FCSTD DOCUMENT  (FreeCAD 1.1R38827 (Git))
Label: composit_stand3_bar_assembly
License: All rights reserved
LicenseURL: http://en.wikipedia.org/wiki/All_rights_reserved
objects: App::Link×4, App::DocumentObjectGroup×3, PartDesign::CoordinateSystem×2, App::FeaturePython×1, App::Part×1
note: 2 computed .brp shape members not serialized (recipe doc carries the construction recipe); baked Part::Feature solids carry a one-line shape summary decoded from their .brp
EXTERNAL_REF file=composit_stand3_bar_model.FCStd obj=Local_CS
EXTERNAL_REF file=composit_stand3_bar_model.FCStd obj=Body
EXTERNAL_REF file=composit_stand3_bar_bottom_model.FCStd obj=Local_CS
EXTERNAL_REF file=composit_stand3_bar_model.FCStd obj=Local_CS001
EXTERNAL_REF file=composit_stand3_bar_bottom_model.FCStd obj=Body
EXTERNAL_REF file=composit_stand3_bar_bottom_model.FCStd obj=Local_CS001
EXTERNAL_REF file=composit_stand3_bar_model.FCStd obj=Local_CS002
EXTERNAL_REF file=composit_stand3_bar_bottom_model.FCStd obj=Body002
EXTERNAL_REF file=composit_stand3_bar_model.FCStd obj=Local_CS004
EXTERNAL_REF file=composit_stand3_bar_top_model.FCStd obj=Local_CS001
EXTERNAL_REF file=composit_stand3_bar_top_model.FCStd obj=Body
EXTERNAL_REF file=composit_stand3_bar_main.FCStd obj=Spreadsheet

FEATURE [App::DocumentObjectGroup] Parts
FEATURE [PartDesign::CoordinateSystem] LCS_Origin
  AttacherType = Attacher::AttachEngine3D
  AttachmentSupport = -> [X_Axis]
  MapMode = 2
FEATURE [App::DocumentObjectGroup] Constraints
FEATURE [App::FeaturePython] Variables  # WARN: FeaturePython — macro-defined, semantics opaque (R4)
  Type = App::PropertyContainer
FEATURE [App::DocumentObjectGroup] Configurations
FEATURE [App::Link] bar001
  AttachedBy = #Local_CS
  AttachedTo = Parent Assembly#LCS_Origin
  LinkedObject = -> <external composit_stand3_bar_model.FCStd>#Body
  SolverId = Asm4EE
  expr: Placement = LCS_Origin.Placement * AttachmentOffset * composit_stand3_bar_model#Local_CS.Placement ^ -1
FEATURE [App::Link] bar_bottom
  AttachedBy = #Local_CS
  AttachedTo = bar001#Local_CS001
  LinkPlacement = pos=(54,18.3,0) rot=(0,0,1;1.5708rad)
  LinkedObject = -> <external composit_stand3_bar_bottom_model.FCStd>#Body
  Placement = pos=(54,18.3,0) rot=(0,0,1;1.5708rad)
  SolverId = Asm4EE
  expr: Placement = bar001.Placement * composit_stand3_bar_model#Local_CS001.Placement * AttachmentOffset * composit_stand3_bar_bottom_model#Local_CS.Placement ^ -1
FEATURE [App::Link] bar_bottom_mirror
  AttachedBy = #Local_CS001
  AttachedTo = bar001#Local_CS002
  LinkPlacement = pos=(54,-18.3,0) rot=(0,0,-1;1.5708rad)
  LinkedObject = -> <external composit_stand3_bar_bottom_model.FCStd>#Body002
  Placement = pos=(54,-18.3,0) rot=(0,0,-1;1.5708rad)
  SolverId = Asm4EE
  expr: Placement = bar001.Placement * composit_stand3_bar_model#Local_CS002.Placement * AttachmentOffset * composit_stand3_bar_bottom_model#Local_CS001.Placement ^ -1
FEATURE [App::Link] top
  AttachedBy = #Local_CS001
  AttachedTo = bar001#Local_CS004
  AttachmentOffset = pos=(0,0,-6) rot=(0,0,1;0rad)
  LinkPlacement = pos=(2,0,1594) rot=(0,0,1;0rad)
  LinkedObject = -> <external composit_stand3_bar_top_model.FCStd>#Body
  Placement = pos=(2,0,1594) rot=(0,0,1;0rad)
  SolverId = Asm4EE
  expr: Placement = bar001.Placement * composit_stand3_bar_model#Local_CS004.Placement * AttachmentOffset * composit_stand3_bar_top_model#Local_CS001.Placement ^ -1
FEATURE [PartDesign::CoordinateSystem] top_LCS
  AttacherType = Attacher::AttachEngine3D
  AttachmentOffset = pos=(0,0,1684) rot=(0,0,1;0rad)
  AttachmentSupport = -> [LCS_Origin]
  MapMode = 5
  Placement = pos=(0,0,1684) rot=(0,0,1;0rad)
  expr: .AttachmentOffset.Base.z = composit_stand3_bar_main#<<Properties>>.height
FEATURE [App::Part] Assembly
  AssemblyType = Part::Link
  Group = -> [LCS_Origin,Constraints,Variables,Configurations,bar001,bar_bottom,bar_bottom_mirror,top,top_LCS]
  Origin = -> Origin
  Type = Assembly

RESOLVED EXTERNAL PARTS (link-assembly join: the EXTERNAL_REF files above that resolve inside this repo's crawl, each included once):
---- part composit_stand3_bar_bottom_model.FCStd = doc fcstd_6c99a19c1178 ----
FCSTD DOCUMENT  (FreeCAD 1.1R38827 (Git))
Label: composit_stand3_bar_bottom_model
License: All rights reserved
LicenseURL: http://en.wikipedia.org/wiki/All_rights_reserved
objects: PartDesign::SubShapeBinder×3, PartDesign::Pad×3, Part::FeaturePython×3, PartDesign::Body×3, App::Link×2, Part::Cylinder×2, PartDesign::CoordinateSystem×2, Part::Mirroring×2, Part::MultiFuse×1, PartDesign::Boolean×1, PartDesign::FeatureBase×1, Part::Feature×1
note: 30 computed .brp shape members not serialized (recipe doc carries the construction recipe); baked Part::Feature solids carry a one-line shape summary decoded from their .brp
EXTERNAL_REF file=composit_stand3_bar_bottom_main.FCStd obj=Sketch
EXTERNAL_REF file=composit_stand3_bar_bottom_main.FCStd obj=Sketch001
EXTERNAL_REF file=composit_stand3_bar_bottom_main.FCStd obj=Sketch002
EXTERNAL_REF file=composit_stand3_bar_bottom_main.FCStd obj=Spreadsheet
EXTERNAL_REF file=composit_stand3_bar_bottom_main.FCStd obj=Join
EXTERNAL_REF file=composit_stand3_bar_bottom_main.FCStd obj=Join001

FEATURE [PartDesign::SubShapeBinder] Binder
  BindCopyOnChange = 0
  BindMode = 0
  ClaimChildren = true
  Context = -> Body [Binder.]
  Fuse = false
  MakeFace = true
  OffsetFill = false
  OffsetIntersection = false
  OffsetJoinType = 0
  OffsetOpenResult = false
  PartialLoad = false
  Relative = true
  Support = -> [<external composit_stand3_bar_bottom_main.FCStd>#Sketch]
  _Version = 2
FEATURE [PartDesign::SubShapeBinder] Binder001
  BindCopyOnChange = 0
  BindMode = 0
  ClaimChildren = true
  Context = -> Body [Binder001.]
  Fuse = false
  MakeFace = true
  OffsetFill = false
  OffsetIntersection = false
  OffsetJoinType = 0
  OffsetOpenResult = false
  PartialLoad = false
  Relative = true
  Support = -> [<external composit_stand3_bar_bottom_main.FCStd>#Sketch001]
  _Version = 2
FEATURE [PartDesign::SubShapeBinder] Binder002
  BindCopyOnChange = 0
  BindMode = 0
  ClaimChildren = true
  Context = -> Body [Binder002.]
  Fuse = false
  MakeFace = true
  OffsetFill = false
  OffsetIntersection = false
  OffsetJoinType = 0
  OffsetOpenResult = false
  PartialLoad = false
  Relative = true
  Support = -> [<external composit_stand3_bar_bottom_main.FCStd>#Sketch002]
  _Version = 2
FEATURE [PartDesign::Pad] Pad
  Direction = (0,1,0)
  Length = 100
  Length2 = 10
  Midplane = true
  Profile = -> Binder
  Suppressed = false
  Type = 0
  expr: Length = <<composit_stand3_bar_bottom_main>>#<<Properties>>.width
FEATURE [PartDesign::Pad] Pad001
  BaseFeature = -> Pad
  Direction = (0,0,1)
  Length = 2
  Length2 = 10
  Profile = -> Binder001
  Suppressed = false
  Type = 0
  expr: Length = <<composit_stand3_bar_bottom_main>>#<<Properties>>.thickness
FEATURE [PartDesign::Pad] Pad002
  BaseFeature = -> Pad001
  Direction = (1,4e-16,0)
  Length = 2
  Length2 = 10
  Profile = -> Binder002
  Refine = true
  Suppressed = false
  Type = 0
  expr: Length = <<composit_stand3_bar_bottom_main>>#<<Properties>>.thickness
FEATURE [App::Link] Link  label="Join"
  LinkedObject = -> <external composit_stand3_bar_bottom_main.FCStd>#Join
FEATURE [App::Link] Link001  label="Join001"
  LinkedObject = -> <external composit_stand3_bar_bottom_main.FCStd>#Join001
FEATURE [Part::Cylinder] Cylinder  label="hole_3.4mm"
  Angle = 360
  AttacherType = Attacher::AttachEngine3D
  FirstAngle = 0
  Height = 10
  Placement = pos=(0,0,0) rot=(1,0,0;3.14159rad)
  Radius = 1.7
  SecondAngle = 0
FEATURE [Part::Cylinder] Cylinder001  label="hole_5.5mm"
  Angle = 360
  AttacherType = Attacher::AttachEngine3D
  FirstAngle = 0
  Height = 10
  Placement = pos=(0,0,0) rot=(1,0,0;3.14159rad)
  Radius = 2.75
  SecondAngle = 0
FEATURE [Part::FeaturePython] Populate  label="Populate Join with hole_5.5mm"  # WARN: FeaturePython — macro-defined, semantics opaque (R4)
  Copying = 0
  ExposePlacement = false
  MarkerShape = 1
  MarkerSize = 0
  NumElements = 0
  Object = -> Cylinder001
  OutputCompounding = 1
  PlacementsTo = -> Link
  Referencing = 0
  Type = lattice2PopulateCopies.LatticePopulateCopies
  isLattice = 0
FEATURE [Part::FeaturePython] Populate001  label="Populate Join001 with hole_3.4mm"  # WARN: FeaturePython — macro-defined, semantics opaque (R4)
  Copying = 0
  ExposePlacement = false
  MarkerShape = 1
  MarkerSize = 0
  NumElements = 0
  Object = -> Cylinder
  OutputCompounding = 1
  PlacementsTo = -> Link001
  Referencing = 0
  Type = lattice2PopulateCopies.LatticePopulateCopies
  isLattice = 0
FEATURE [PartDesign::Body] Body001
  AllowCompound = false
  Origin = -> Origin001
FEATURE [Part::MultiFuse] Fusion
  Shapes = -> [Populate,Populate001]
FEATURE [PartDesign::Boolean] Boolean
  BaseFeature = -> Pad002
  Group = -> [Fusion]
  Suppressed = false
  Type = 1
  UsePlacement = true
FEATURE [PartDesign::CoordinateSystem] Local_CS  label="LCS"
  AttacherType = Attacher::AttachEngine3D
  AttachmentSupport = -> [XY_Plane]
  MapMode = 5
FEATURE [PartDesign::Body] Body  label="bar_bottom"
  AllowCompound = false
  Group = -> [Binder,Binder001,Binder002,Pad,Pad001,Pad002,Boolean,Local_CS]
  Origin = -> Origin
  Tip = -> Boolean
FEATURE [Part::FeaturePython] Clone  label="bar_bottom001"  # Draft clone (typed FeaturePython)
  AttacherType = Attacher::AttachEngine3D
  Fuse = false
  Objects = -> [Body]
  Scale = (1,1,1)
FEATURE [Part::Mirroring] Part__Mirroring  label="bar_bottom001 (Mirror #1)"
  Base = (0,0,0)
  Normal = (0,1,0)
  Source = -> Clone
FEATURE [PartDesign::FeatureBase] BaseFeature
  BaseFeature = -> Part__Mirroring
  Suppressed = false
FEATURE [PartDesign::CoordinateSystem] Local_CS001  label="bar_bottom_mirror_LCS"
  AttacherType = Attacher::AttachEngine3D
  AttachmentSupport = -> [XY_Plane002]
  MapMode = 5
FEATURE [PartDesign::Body] Body002  label="bar_bottom_mirror"
  AllowCompound = false
  BaseFeature = -> Part__Mirroring
  Group = -> [BaseFeature,Local_CS001]
  Origin = -> Origin002
  Tip = -> BaseFeature
FEATURE [Part::Feature] Body163  label="pillar_bottom_material_0.30ansi002"
  Placement = pos=(0,0,0) rot=(0,0,1;1.5708rad)
  shape: bbox 25 x 100 x 80 mm, 23 faces (baked)
FEATURE [Part::Mirroring] Part__Mirroring001  label="pillar_bottom_material_0.30ansi002 (Mirror #2)"
  Base = (0,0,0)
  Normal = (0,1,0)
  Source = -> Body163
---- part composit_stand3_bar_main.FCStd = doc fcstd_660642a5c5ee ----
FCSTD DOCUMENT  (FreeCAD 1.1R38827 (Git))
Label: composit_stand3_bar_main
License: All rights reserved
LicenseURL: http://en.wikipedia.org/wiki/All_rights_reserved
objects: Part::FeaturePython×4, Sketcher::SketchObject×2, Spreadsheet::Sheet×1, PartDesign::SubShapeBinder×1
note: 9 computed .brp shape members not serialized (recipe doc carries the construction recipe); baked Part::Feature solids carry a one-line shape summary decoded from their .brp
EXTERNAL_REF file=composit_stand3_bar_bottom_main.FCStd obj=Spreadsheet
EXTERNAL_REF file=../ULZ-P02-14W.FCStd obj=Sketch

FEATURE [Sketcher::SketchObject] Sketch  label="base_Sketch"
  ArcFitTolerance = 0
  FullyConstrained = true
  MakeInternals = false
  expr: .Constraints.length = <<Properties>>.length
  expr: .Constraints.width = <<Properties>>.width
  sketch-geometry (5):
    g0: LineSegment StartX=19 StartY=18.3 StartZ=0 EndX=0 EndY=18.3 EndZ=0
    g1: LineSegment StartX=0 StartY=18.3 StartZ=0 EndX=0 EndY=-18.3 EndZ=0
    g2: LineSegment StartX=0 StartY=-18.3 StartZ=0 EndX=19 EndY=-18.3 EndZ=0
    g3: LineSegment [constr] StartX=19 StartY=-18.3 StartZ=0 EndX=19 EndY=18.3 EndZ=0
    g4: GeomPoint [constr] X=9.5 Y=0 Z=0
  constraints (13):
    c: Coincident(g0,g1)
    c: Coincident(g1,g2)
    c: Coincident(g2,g3)
    c: Coincident(g3,g0)
    c: Horizontal(g0)
    c: Horizontal(g2)
    c: Vertical(g1)
    c: Vertical(g3)
    c: Symmetric(g2,g0,g4)
    c: PointOnObject(g4,g-1)
    c: PointOnObject(g1,g-2)
    c: DistanceX(g1,g0) = 19  'length'
    c: DistanceY(g1,g0) = 36.6  'width'
FEATURE [Spreadsheet::Sheet] Spreadsheet  label="Properties"
  cells = B2(width)==36.6 mm; C2(length)==19 mm; D2(height)==1684 mm; E2(thickness)==2 mm
FEATURE [Part::FeaturePython] Placment  label="bottom_placement"  # WARN: FeaturePython — macro-defined, semantics opaque (R4)
  AttacherType = Attacher::AttachEngine3D
  ExposePlacement = true
  MarkerShape = 1
  MarkerSize = 10
  NumElements = 1
  Placement = pos=(54,18.3,0) rot=(0,0,1;1.5708rad)
  Type = lattice2AttachablePlacement.AttachablePlacement
  isLattice = 1
  expr: .Placement.Base.x = <<composit_stand3_bar_bottom_main>>#<<Properties>>.width / 2 + 4 mm
  expr: .Placement.Base.y = <<Properties>>.width / 2
FEATURE [Part::FeaturePython] Placment001  label="bottom_placement2"  # WARN: FeaturePython — macro-defined, semantics opaque (R4)
  AttacherType = Attacher::AttachEngine3D
  ExposePlacement = true
  MarkerShape = 1
  MarkerSize = 10
  NumElements = 1
  Placement = pos=(54,-18.3,0) rot=(0,0,-1;1.5708rad)
  Type = lattice2AttachablePlacement.AttachablePlacement
  isLattice = 1
  expr: .Placement.Base.x = <<bottom_placement>>.Placement.Base.x
  expr: .Placement.Base.y = -<<bottom_placement>>.Placement.Base.y
FEATURE [Part::FeaturePython] Placment003  label="lamp_placement"  # WARN: FeaturePython — macro-defined, semantics opaque (R4)
  AttacherType = Attacher::AttachEngine3D
  ExposePlacement = true
  MarkerShape = 1
  MarkerSize = 20
  NumElements = 1
  Placement = pos=(0,0,1060) rot=(0.57735,0.57735,0.57735;2.0944rad)
  Type = lattice2AttachablePlacement.AttachablePlacement
  isLattice = 1
  expr: .Placement.Base.z = <<Properties>>.height - 624 mm
FEATURE [Part::FeaturePython] Placment004  label="top_part_placement"  # WARN: FeaturePython — macro-defined, semantics opaque (R4)
  AttacherType = Attacher::AttachEngine3D
  ExposePlacement = true
  MarkerShape = 1
  MarkerSize = 20
  NumElements = 1
  Placement = pos=(2,0,1678) rot=(0,0,1;0rad)
  Type = lattice2AttachablePlacement.AttachablePlacement
  isLattice = 1
  expr: .Placement.Base.x = <<Properties>>.thickness
  expr: .Placement.Base.z = <<Properties>>.height - 6 mm
FEATURE [PartDesign::SubShapeBinder] Binder  label="lamp_holes_import"
  BindCopyOnChange = 0
  BindMode = 0
  ClaimChildren = false
  Fuse = false
  MakeFace = true
  OffsetFill = false
  OffsetIntersection = false
  OffsetJoinType = 0
  OffsetOpenResult = false
  PartialLoad = false
  Relative = true
  Support = -> [<external ../ULZ-P02-14W.FCStd>#Sketch]
  _Version = 2
FEATURE [Sketcher::SketchObject] Sketch001  label="lamp_holes_sketch"
  ArcFitTolerance = 0
  ExternalGeometry = -> [Binder]
  FullyConstrained = true
  MakeInternals = false
  sketch-geometry (12):
    g0: Circle CenterX=-4.15 CenterY=445 CenterZ=0 NormalX=0 NormalY=0 NormalZ=1 AngleXU=0 Radius=1.7
    g1: Circle CenterX=4.15 CenterY=445 CenterZ=0 NormalX=0 NormalY=0 NormalZ=1 AngleXU=0 Radius=1.7
    g2: ArcOfCircle CenterX=4.15 CenterY=-446 CenterZ=0 NormalX=0 NormalY=0 NormalZ=1 AngleXU=0 Radius=1.7 StartAngle=3.14159 EndAngle=6.28319
    g3: ArcOfCircle CenterX=4.15 CenterY=-444 CenterZ=0 NormalX=0 NormalY=0 NormalZ=1 AngleXU=0 Radius=1.7 StartAngle=-2.7e-15 EndAngle=3.14159
    g4: LineSegment StartX=2.45 StartY=-446 StartZ=0 EndX=2.45 EndY=-444 EndZ=0
    g5: LineSegment StartX=5.85 StartY=-446 StartZ=0 EndX=5.85 EndY=-444 EndZ=0
    g6: ArcOfCircle CenterX=-4.15 CenterY=-446 CenterZ=0 NormalX=0 NormalY=0 NormalZ=1 AngleXU=0 Radius=1.7 StartAngle=3.14159 EndAngle=6.28319
    g7: ArcOfCircle CenterX=-4.15 CenterY=-444 CenterZ=0 NormalX=0 NormalY=0 NormalZ=1 AngleXU=0 Radius=1.7 StartAngle=1.11e-14 EndAngle=3.14159
    g8: LineSegment StartX=-5.85 StartY=-446 StartZ=0 EndX=-5.85 EndY=-444 EndZ=0
    g9: LineSegment StartX=-2.45 StartY=-446 StartZ=0 EndX=-2.45 EndY=-444 EndZ=0
    g10: LineSegment [constr] StartX=4.15 StartY=-446 StartZ=0 EndX=4.15 EndY=-445 EndZ=0
    g11: LineSegment [constr] StartX=4.15 StartY=-445 StartZ=0 EndX=4.15 EndY=-444 EndZ=0
  constraints (26):
    c: Coincident(g0,g-3)
    c: Tangent(g2,g4) = 1.5708
    c: Tangent(g2,g5) = -1.5708
    c: Tangent(g3,g4) = 1.5708
    c: Tangent(g3,g5) = -1.5708
    c: Equal(g2,g3)
    c: Vertical(g4)
    c: Tangent(g6,g8) = 1.5708
    c: Tangent(g6,g9) = -1.5708
    c: Tangent(g7,g8) = 1.5708
    c: Tangent(g7,g9) = -1.5708
    c: Equal(g6,g7)
    c: Equal(g7,g3)
    c: Equal(g0,g1)
    c: Diameter(g0) = 3.4
    c: Symmetric(g1,g0,g-2)
    c: Symmetric(g3,g7,g-2)
    c: Symmetric(g6,g2,g-2)
    c: Coincident(g10,g2)
    c: Coincident(g10,g-4)
    c: Vertical(g10)
    c: Coincident(g10,g11)
    c: Coincident(g11,g3)
    c: DistanceY(g10,g10) = 1
    c: DistanceY(g11,g11) = 1
    c: Equal(g7,g0)
---- part composit_stand3_bar_model.FCStd = doc fcstd_abfcac44bc21 ----
FCSTD DOCUMENT  (FreeCAD 1.1R38827 (Git))
Label: composit_stand3_bar_model
License: All rights reserved
LicenseURL: http://en.wikipedia.org/wiki/All_rights_reserved
objects: App::Link×8, Part::FeaturePython×7, PartDesign::CoordinateSystem×5, PartDesign::SubShapeBinder×3, Part::Extrusion×2, Part::Mirroring×2, PartDesign::Body×2, PartDesign::FeaturePython×1, Sketcher::SketchObject×1, Part::Compound×1, Part::Cylinder×1, Part::Feature×1, Part::MultiFuse×1, PartDesign::Boolean×1
note: 31 computed .brp shape members not serialized (recipe doc carries the construction recipe); baked Part::Feature solids carry a one-line shape summary decoded from their .brp
EXTERNAL_REF file=composit_stand3_bar_main.FCStd obj=Sketch
EXTERNAL_REF file=composit_stand3_bar_main.FCStd obj=Spreadsheet
EXTERNAL_REF file=composit_stand3_bar_bottom_main.FCStd obj=Join001
EXTERNAL_REF file=composit_stand3_bar_main.FCStd obj=Placment
EXTERNAL_REF file=composit_stand3_bar_main.FCStd obj=Placment001
EXTERNAL_REF file=composit_stand3_bar_main.FCStd obj=Sketch001
EXTERNAL_REF file=composit_stand3_bar_main.FCStd obj=Placment003
EXTERNAL_REF file=composit_stand3_plexiglass_outer_main.FCStd obj=Spreadsheet
EXTERNAL_REF file=composit_stand3_plexiglass_outer_main.FCStd obj=LinearArray
EXTERNAL_REF file=composit_stand3_main.FCStd obj=Cylinder001
EXTERNAL_REF file=composit_stand3_bar_top_main.FCStd obj=Join
EXTERNAL_REF file=composit_stand3_bar_main.FCStd obj=Placment004

FEATURE [PartDesign::SubShapeBinder] Binder
  BindCopyOnChange = 0
  BindMode = 0
  ClaimChildren = true
  Fuse = false
  MakeFace = true
  OffsetFill = false
  OffsetIntersection = false
  OffsetJoinType = 0
  OffsetOpenResult = false
  PartialLoad = false
  Relative = false
  Support = -> [<external composit_stand3_bar_main.FCStd>#Sketch]
  _Version = 2
FEATURE [PartDesign::SubShapeBinder] Binder001
  BindCopyOnChange = 0
  BindMode = 0
  ClaimChildren = true
  Context = -> Body [Binder001.]
  Fuse = false
  MakeFace = true
  OffsetFill = false
  OffsetIntersection = false
  OffsetJoinType = 0
  OffsetOpenResult = false
  PartialLoad = false
  Relative = false
  Support = -> [Binder]
  _Version = 2
FEATURE [PartDesign::FeaturePython] BaseBend  # WARN: FeaturePython — macro-defined, semantics opaque (R4)
  BendSide = 1
  BendSketch = -> Binder001
  MidPlane = false
  Reverse = false
  Suppressed = false
  length = 1684
  radius = 2
  thickness = 2
  expr: length = <<composit_stand3_bar_main>>#<<Properties>>.height
  expr: thickness = <<composit_stand3_bar_main>>#<<Properties>>.thickness
FEATURE [Sketcher::SketchObject] Sketch
  ArcFitTolerance = 0
  FullyConstrained = true
  MakeInternals = false
  sketch-geometry (3):
    g0: LineSegment StartX=0 StartY=5 StartZ=0 EndX=0 EndY=0 EndZ=0
    g1: LineSegment StartX=0 StartY=0 StartZ=0 EndX=5 EndY=7.2253e-12 EndZ=0
    g2: ArcOfCircle CenterX=5 CenterY=5 CenterZ=0 NormalX=0 NormalY=0 NormalZ=1 AngleXU=0 Radius=5 StartAngle=3.14159 EndAngle=4.71239
  constraints (7):
    c: PointOnObject(g0,g-2)
    c: Coincident(g0,g-1)
    c: Coincident(g0,g1)
    c: PointOnObject(g1,g-1)
    c: Tangent(g2,g0) = -1.5708
    c: Tangent(g2,g1) = -1.5708
    c: Radius(g2) = 5
FEATURE [Part::Extrusion] Extrude
  Base = -> Sketch
  Dir = (0,0,1)
  DirMode = 2
  FaceMakerClass = Part::FaceMakerBullseye
  FaceMakerMode = 3
  LengthFwd = 10
  LengthRev = 0
  Solid = true
  Symmetric = false
FEATURE [Part::FeaturePython] Placment  # WARN: FeaturePython — macro-defined, semantics opaque (R4)
  AttacherType = Attacher::AttachEngine3D
  ExposePlacement = true
  MarkerShape = 1
  MarkerSize = 5
  NumElements = 1
  Placement = pos=(19,-18.3,0) rot=(0,0.707107,0.707107;3.14159rad)
  Type = lattice2AttachablePlacement.AttachablePlacement
  isLattice = 1
  expr: .Placement.Base.x = <<composit_stand3_bar_main>>#<<Properties>>.length
  expr: .Placement.Base.y = -<<composit_stand3_bar_main>>#<<Properties>>.width / 2
FEATURE [Part::FeaturePython] Populate  label="Populate Placment with Extrude"  # WARN: FeaturePython — macro-defined, semantics opaque (R4)
  Copying = 0
  ExposePlacement = false
  MarkerShape = 1
  MarkerSize = 0
  NumElements = 0
  Object = -> Extrude
  OutputCompounding = 2
  PlacementsTo = -> Placment
  Referencing = 0
  Type = lattice2PopulateCopies.LatticePopulateCopies
  isLattice = 0
FEATURE [Part::Mirroring] Part__Mirroring  label="Populate Placment with Extrude (Mirror #1)"
  Base = (0,0,0)
  Normal = (0,1,0)
  Source = -> Populate
FEATURE [Part::Compound] Compound
  Links = -> [Populate,Part__Mirroring]
FEATURE [Part::Mirroring] Part__Mirroring001  label="Compound (Mirror #2)"
  Base = (0,0,842)
  Normal = (0,0,1)
  Source = -> Compound
  expr: .Base.z = <<composit_stand3_bar_main>>#<<Properties>>.height / 2
FEATURE [PartDesign::Body] Body001
  AllowCompound = false
  Origin = -> Origin001
FEATURE [App::Link] Link  label="Join001"
  LinkedObject = -> <external composit_stand3_bar_bottom_main.FCStd>#Join001
FEATURE [App::Link] Link001  label="bottom_placement"
  LinkTransform = true
  LinkedObject = -> <external composit_stand3_bar_main.FCStd>#Placment
FEATURE [Part::FeaturePython] Populate001  label="Populate bottom_placement with Join001"  # WARN: FeaturePython — macro-defined, semantics opaque (R4)
  Copying = 0
  ExposePlacement = false
  MarkerShape = 1
  MarkerSize = 0
  NumElements = 3
  Object = -> Link
  OutputCompounding = 0
  PlacementsTo = -> Link001
  Referencing = 0
  Type = lattice2PopulateCopies.LatticePopulateCopies
  isLattice = 1
FEATURE [Part::FeaturePython] Mirror  label="Mirror of Populate bottom_placement with Join001"  # WARN: FeaturePython — macro-defined, semantics opaque (R4)
  ExposePlacement = false
  FlipX = false
  FlipY = true
  FlipZ = false
  MarkerShape = 1
  MarkerSize = 0
  NumElements = 3
  Object = -> Populate001
  ObjectTraversal = 0
  Type = lattice2Mirror.LatticeMirror
  isLattice = 1
FEATURE [Part::Cylinder] Cylinder
  Angle = 360
  AttacherType = Attacher::AttachEngine3D
  FirstAngle = 0
  Height = 10
  Placement = pos=(0,0,0) rot=(1,0,0;3.14159rad)
  Radius = 1.7
  SecondAngle = 0
FEATURE [PartDesign::CoordinateSystem] Local_CS  label="base_LCS"
  AttacherType = Attacher::AttachEngine3D
  AttachmentSupport = -> [XY_Plane]
  MapMode = 5
FEATURE [PartDesign::CoordinateSystem] Local_CS001  label="bottom1_LCS"
  AttacherType = Attacher::AttachEngine3D
  AttachmentOffset = pos=(54,18.3,0) rot=(0,0,1;1.5708rad)
  AttachmentSupport = -> [XY_Plane]
  MapMode = 5
  Placement = pos=(54,18.3,0) rot=(0,0,1;1.5708rad)
  expr: AttachmentOffset = <<bottom_placement>>.LinkedObject.Placement
FEATURE [App::Link] Link002  label="bottom_placement2"
  LinkTransform = true
  LinkedObject = -> <external composit_stand3_bar_main.FCStd>#Placment001
FEATURE [PartDesign::CoordinateSystem] Local_CS002  label="bottom2_LCS"
  AttacherType = Attacher::AttachEngine3D
  AttachmentOffset = pos=(54,-18.3,0) rot=(0,0,-1;1.5708rad)
  AttachmentSupport = -> [XY_Plane]
  MapMode = 5
  Placement = pos=(54,-18.3,0) rot=(0,0,-1;1.5708rad)
  expr: AttachmentOffset = <<bottom_placement2>>.LinkedObject.Placement
FEATURE [PartDesign::SubShapeBinder] Binder002  label="lamp_holes"
  BindCopyOnChange = 0
  BindMode = 0
  ClaimChildren = false
  Fuse = false
  MakeFace = true
  OffsetFill = false
  OffsetIntersection = false
  OffsetJoinType = 0
  OffsetOpenResult = false
  PartialLoad = false
  Relative = true
  Support = -> [<external composit_stand3_bar_main.FCStd>#Sketch001]
  _Version = 2
FEATURE [App::Link] Link003  label="lamp_placement"
  LinkTransform = true
  LinkedObject = -> <external composit_stand3_bar_main.FCStd>#Placment003
FEATURE [Part::Extrusion] Extrude001
  Base = -> Binder002
  Dir = (0,0,1)
  DirMode = 2
  FaceMakerClass = Part::FaceMakerBullseye
  FaceMakerMode = 3
  LengthFwd = 10
  LengthRev = 0
  Reversed = true
  Solid = false
  Symmetric = true
FEATURE [Part::FeaturePython] Populate003  label="Populate lamp_placement with Extrude001"  # WARN: FeaturePython — macro-defined, semantics opaque (R4)
  Copying = 0
  ExposePlacement = false
  MarkerShape = 1
  MarkerSize = 0
  NumElements = 0
  Object = -> Extrude001
  OutputCompounding = 2
  PlacementsTo = -> Link003
  Referencing = 0
  Type = lattice2PopulateCopies.LatticePopulateCopies
  isLattice = 0
FEATURE [Part::Feature] Body164  label="pillar004"
  Placement = pos=(0,0,0) rot=(0,0,-1;1.5708rad)
  shape: bbox 19 x 36.6 x 1684 mm, 63 faces (baked)
FEATURE [App::Link] Link004  label="bar_fix_placements"
  LinkPlacement = pos=(-1,0,474) rot=(0,0,1;0rad)
  LinkTransform = true
  LinkedObject = -> <external composit_stand3_plexiglass_outer_main.FCStd>#LinearArray
  Placement = pos=(-1,0,474) rot=(0,0,1;0rad)
  expr: .Placement.Base.z = composit_stand3_bar_main#<<Properties>>.height - composit_stand3_plexiglass_outer_main#<<Properties>>.height
FEATURE [PartDesign::CoordinateSystem] Local_CS003  label="top_LCS"
  AttacherType = Attacher::AttachEngine3D
  AttachmentOffset = pos=(0,0,1684) rot=(0,0,1;0rad)
  AttachmentSupport = -> [XY_Plane]
  MapMode = 5
  Placement = pos=(0,0,1684) rot=(0,0,1;0rad)
  expr: .AttachmentOffset.Base.z = <<BaseBend>>.length
FEATURE [PartDesign::CoordinateSystem] Local_CS004  label="top_inner_LCS"
  AttacherType = Attacher::AttachEngine3D
  AttachmentOffset = pos=(2,0,1684) rot=(0,0,1;0rad)
  AttachmentSupport = -> [XY_Plane]
  MapMode = 5
  Placement = pos=(2,0,1684) rot=(0,0,1;0rad)
  expr: .AttachmentOffset.Base.x = <<BaseBend>>.thickness
  expr: .AttachmentOffset.Base.z = <<BaseBend>>.length
FEATURE [App::Link] Link005  label="hole_3.4mm_rev"
  LinkTransform = true
  LinkedObject = -> <external composit_stand3_main.FCStd>#Cylinder001
FEATURE [Part::FeaturePython] Join001  label="Join002"  # WARN: FeaturePython — macro-defined, semantics opaque (R4)
  ExposePlacement = false
  Interleave = false
  Links = -> [Populate001,Mirror,Link004]
  MarkerShape = 1
  MarkerSize = 0
  NumElements = 11
  Type = lattice2JoinArrays.JoinArrays
  isLattice = 1
FEATURE [Part::FeaturePython] Populate005  label="Populate Join002 with hole_3.4mm_rev"  # WARN: FeaturePython — macro-defined, semantics opaque (R4)
  Copying = 0
  ExposePlacement = false
  MarkerShape = 1
  MarkerSize = 0
  NumElements = 0
  Object = -> Link005
  OutputCompounding = 1
  PlacementsTo = -> Join001
  Referencing = 0
  Type = lattice2PopulateCopies.LatticePopulateCopies
  isLattice = 0
FEATURE [Part::MultiFuse] Fusion
  Shapes = -> [Compound,Part__Mirroring001,Populate003,Populate005]
FEATURE [PartDesign::Boolean] Boolean
  BaseFeature = -> BaseBend
  Group = -> [Fusion]
  Suppressed = false
  Type = 1
  UsePlacement = true
FEATURE [PartDesign::Body] Body  label="bar"
  AllowCompound = false
  Group = -> [Binder001,BaseBend,Boolean,Local_CS,Local_CS001,Local_CS002,Local_CS003,Local_CS004]
  Origin = -> Origin
  Tip = -> Boolean
FEATURE [App::Link] Link006  label="vert_holes"
  LinkedObject = -> <external composit_stand3_bar_top_main.FCStd>#Join
FEATURE [App::Link] Link007  label="top_part_placement"
  LinkClaimChild = true
  LinkTransform = true
  LinkedObject = -> <external composit_stand3_bar_main.FCStd>#Placment004
---- part composit_stand3_bar_top_model.FCStd = doc fcstd_d625f469b094 ----
FCSTD DOCUMENT  (FreeCAD 1.1R38827 (Git))
Label: composit_stand3_bar_top_model
License: All rights reserved
LicenseURL: http://en.wikipedia.org/wiki/All_rights_reserved
objects: Sketcher::SketchObject×4, PartDesign::Pocket×4, PartDesign::SubShapeBinder×2, App::Link×2, Part::FeaturePython×2, PartDesign::Body×2, PartDesign::CoordinateSystem×2, PartDesign::FeaturePython×1, PartDesign::Mirrored×1, Part::Cylinder×1, Part::MultiFuse×1, PartDesign::Boolean×1
note: 36 computed .brp shape members not serialized (recipe doc carries the construction recipe); baked Part::Feature solids carry a one-line shape summary decoded from their .brp
EXTERNAL_REF file=composit_stand3_bar_top_main.FCStd obj=Sketch
EXTERNAL_REF file=composit_stand3_bar_top_main.FCStd obj=Join001
EXTERNAL_REF file=composit_stand3_bar_top_main.FCStd obj=Join

FEATURE [PartDesign::SubShapeBinder] Binder
  BindCopyOnChange = 0
  BindMode = 0
  ClaimChildren = true
  Fuse = false
  MakeFace = true
  OffsetFill = false
  OffsetIntersection = false
  OffsetJoinType = 0
  OffsetOpenResult = false
  PartialLoad = false
  Placement = pos=(0,0,0) rot=(1,0,0;1.5708rad)
  Relative = false
  Support = -> [<external composit_stand3_bar_top_main.FCStd>#Sketch]
  _Version = 2
FEATURE [PartDesign::SubShapeBinder] Binder001
  BindCopyOnChange = 0
  BindMode = 0
  ClaimChildren = true
  Context = -> Body [Binder001.]
  Fuse = false
  MakeFace = true
  OffsetFill = false
  OffsetIntersection = false
  OffsetJoinType = 0
  OffsetOpenResult = false
  PartialLoad = false
  Placement = pos=(0,0,0) rot=(1,0,0;1.5708rad)
  Relative = false
  Support = -> [Binder]
  _Version = 2
FEATURE [PartDesign::FeaturePython] BaseBend  # WARN: FeaturePython — macro-defined, semantics opaque (R4)
  BendSide = 0
  BendSketch = -> Binder001
  MidPlane = true
  Reverse = true
  Suppressed = false
  length = 28.6
  radius = 2
  thickness = 1
FEATURE [Sketcher::SketchObject] Sketch
  ArcFitTolerance = 0
  AttachmentOffset = pos=(0,-14.3,0) rot=(0,0,1;0rad)
  AttachmentSupport = -> [XY_Plane]
  FullyConstrained = true
  MakeInternals = false
  MapMode = 5
  Placement = pos=(0,-14.3,0) rot=(0,0,1;0rad)
  expr: .AttachmentOffset.Base.y = -<<BaseBend>>.length / 2
  sketch-geometry (7):
    g0: LineSegment StartX=0 StartY=0 StartZ=0 EndX=17 EndY=0 EndZ=0
    g1: LineSegment StartX=9 StartY=9.3 StartZ=0 EndX=0 EndY=9.3 EndZ=0
    g2: LineSegment StartX=0 StartY=9.3 StartZ=0 EndX=0 EndY=0 EndZ=0
    g3: ArcOfCircle CenterX=9 CenterY=4.3 CenterZ=0 NormalX=0 NormalY=0 NormalZ=1 AngleXU=0 Radius=5 StartAngle=0 EndAngle=1.5708
    g4: GeomPoint [constr] X=14 Y=9.3 Z=0
    g5: LineSegment StartX=14 StartY=3 StartZ=0 EndX=14 EndY=4.3 EndZ=0
    g6: ArcOfCircle CenterX=17 CenterY=3 CenterZ=0 NormalX=0 NormalY=0 NormalZ=1 AngleXU=0 Radius=3 StartAngle=3.14159 EndAngle=4.71239
  constraints (17):
    c: Coincident(g1,g2)
    c: Coincident(g2,g0)
    c: Horizontal(g0)
    c: Horizontal(g1)
    c: Vertical(g2)
    c: Coincident(g0,g-1)
    c: PointOnObject(g4,g1)
    c: Tangent(g1,g3) = -1.5708
    c: Radius(g3) = 5
    c: DistanceX(g4) = 14
    c: DistanceY(g4) = 9.3
    c: Vertical(g5)
    c: Tangent(g6,g5) = 1.5708
    c: Tangent(g6,g0) = -1.5708
    c: Radius(g6) = 3
    c: PointOnObject(g4,g5)
    c: Tangent(g5,g3) = -1.5708
FEATURE [PartDesign::Pocket] Pocket
  BaseFeature = -> BaseBend
  Direction = (0,0,-1)
  Length = 3
  Length2 = 5
  Profile = -> Sketch
  ReferenceAxis = -> Sketch [N_Axis]
  Reversed = true
  Suppressed = false
  Type = 0
  expr: Length = <<BaseBend>>.thickness + <<BaseBend>>.radius
FEATURE [Sketcher::SketchObject] Sketch001
  ArcFitTolerance = 0
  AttachmentOffset = pos=(14.3,0,0) rot=(1,0,0;-1.5708rad)
  AttachmentSupport = -> [Binder]
  FullyConstrained = true
  MakeInternals = false
  MapMode = 7
  Placement = pos=(70,14.3,0) rot=(0,0,-1;4.71239rad)
  expr: .AttachmentOffset.Base.x = <<BaseBend>>.length / 2
  sketch-geometry (3):
    g0: ArcOfCircle CenterX=-5 CenterY=5 CenterZ=0 NormalX=0 NormalY=0 NormalZ=1 AngleXU=0 Radius=5 StartAngle=4.71239 EndAngle=6.28319
    g1: LineSegment StartX=-5 StartY=1.981e-13 StartZ=0 EndX=-1.981e-13 EndY=1.981e-13 EndZ=0
    g2: LineSegment StartX=-1.981e-13 StartY=1.981e-13 StartZ=0 EndX=-1.981e-13 EndY=5 EndZ=0
  constraints (8):
    c: PointOnObject(g0,g-2)
    c: PointOnObject(g0,g-1)
    c: Coincident(g1,g2)
    c: Vertical(g2)
    c: Tangent(g2,g0) = -1.5708
    c: Tangent(g0,g1) = -1.5708
    c: Horizontal(g1)
    c: Radius(g0) = 5
FEATURE [Sketcher::SketchObject] Sketch002
  ArcFitTolerance = 0
  AttachmentOffset = pos=(-14.3,0,0) rot=(-0.57735,0.57735,0.57735;2.0944rad)
  AttachmentSupport = -> [Binder]
  FullyConstrained = true
  MakeInternals = false
  MapMode = 7
  Placement = pos=(30,14.3,84) rot=(0,0,1;0rad)
  expr: .AttachmentOffset.Base.x = -<<BaseBend>>.length / 2
  sketch-geometry (3):
    g0: ArcOfCircle CenterX=-2 CenterY=-2 CenterZ=0 NormalX=0 NormalY=0 NormalZ=1 AngleXU=0 Radius=2 StartAngle=0 EndAngle=1.5708
    g1: LineSegment StartX=0 StartY=-2 StartZ=0 EndX=0 EndY=0 EndZ=0
    g2: LineSegment StartX=0 StartY=0 StartZ=0 EndX=-2 EndY=0 EndZ=0
  constraints (7):
    c: PointOnObject(g0,g-2)
    c: PointOnObject(g0,g-1)
    c: Tangent(g1,g0) = -1.5708
    c: Coincident(g1,g-1)
    c: Coincident(g2,g1)
    c: Tangent(g2,g0) = -1.5708
    c: Radius(g0) = 2
FEATURE [PartDesign::Pocket] Pocket001
  BaseFeature = -> Pocket
  Direction = (-1e-16,3e-16,-1)
  Length = 5
  Length2 = 5
  Profile = -> Sketch002
  ReferenceAxis = -> Sketch002 [N_Axis]
  Suppressed = false
  Type = 0
FEATURE [PartDesign::Pocket] Pocket002
  BaseFeature = -> Pocket001
  Direction = (2e-16,0,-1)
  Length = 5
  Length2 = 5
  Profile = -> Sketch001
  ReferenceAxis = -> Sketch001 [N_Axis]
  Reversed = true
  Suppressed = false
  Type = 0
FEATURE [PartDesign::Mirrored] Mirrored
  BaseFeature = -> Pocket002
  MirrorPlane = -> XZ_Plane
  Originals = -> [Pocket001,Pocket002]
  Suppressed = false
  TransformMode = 0
FEATURE [Sketcher::SketchObject] Sketch003
  ArcFitTolerance = 0
  AttachmentOffset = pos=(0,3,0) rot=(0,0,1;0rad)
  AttachmentSupport = -> [YZ_Plane]
  ExternalGeometry = -> [Sketch]
  FullyConstrained = true
  MakeInternals = false
  MapMode = 5
  Placement = pos=(0,0,3) rot=(0.57735,0.57735,0.57735;2.0944rad)
  expr: .AttachmentOffset.Base.y = <<BaseBend>>.thickness + <<BaseBend>>.radius
  sketch-geometry (5):
    g0: LineSegment StartX=-14.3 StartY=4 StartZ=0 EndX=-14.3 EndY=0 EndZ=0
    g1: LineSegment StartX=-14.3 StartY=0 StartZ=0 EndX=-5 EndY=0 EndZ=0
    g2: LineSegment StartX=-6 StartY=1 StartZ=0 EndX=-11.3 EndY=1 EndZ=0
    g3: ArcOfCircle CenterX=-11.3 CenterY=4 CenterZ=0 NormalX=0 NormalY=0 NormalZ=1 AngleXU=0 Radius=3 StartAngle=3.14159 EndAngle=4.71239
    g4: ArcOfCircle CenterX=-6 CenterY=0 CenterZ=0 NormalX=0 NormalY=0 NormalZ=1 AngleXU=0 Radius=1 StartAngle=0 EndAngle=1.5708
  constraints (14):
    c: Vertical(g0)
    c: Coincident(g0,g1)
    c: Horizontal(g1)
    c: Horizontal(g2)
    c: PointOnObject(g4,g1)
    c: Coincident(g4,g1)
    c: Vertical(g-3,g1)
    c: Vertical(g-3,g0)
    c: Tangent(g3,g0) = -1.5708
    c: Tangent(g3,g2) = 1.5708
    c: Tangent(g4,g2) = -1.5708
    c: PointOnObject(g0,g-1)
    c: Radius(g3) = 3
    c: Radius(g4) = 1
FEATURE [PartDesign::Pocket] Pocket003
  BaseFeature = -> Mirrored
  Direction = (-1,0,0)
  Length = 5
  Length2 = 5
  Profile = -> Sketch003
  ReferenceAxis = -> Sketch003 [N_Axis]
  Reversed = true
  Suppressed = false
  Type = 0
FEATURE [App::Link] Link  label="hor_holes"
  LinkedObject = -> <external composit_stand3_bar_top_main.FCStd>#Join001
FEATURE [App::Link] Link001  label="vert_holes"
  LinkedObject = -> <external composit_stand3_bar_top_main.FCStd>#Join
FEATURE [Part::Cylinder] Cylinder
  Angle = 360
  AttacherType = Attacher::AttachEngine3D
  AttachmentOffset = pos=(0,0,0) rot=(1,0,0;3.14159rad)
  FirstAngle = 0
  Height = 10
  Placement = pos=(0,0,0) rot=(1,0,0;3.14159rad)
  Radius = 1.7
  SecondAngle = 0
FEATURE [Part::FeaturePython] Join  # WARN: FeaturePython — macro-defined, semantics opaque (R4)
  ExposePlacement = false
  Interleave = false
  Links = -> [Link,Link001]
  MarkerShape = 1
  MarkerSize = 0
  NumElements = 4
  Type = lattice2JoinArrays.JoinArrays
  isLattice = 1
FEATURE [Part::FeaturePython] Populate  label="Populate Join with Cylinder"  # WARN: FeaturePython — macro-defined, semantics opaque (R4)
  Copying = 0
  ExposePlacement = false
  MarkerShape = 1
  MarkerSize = 0
  NumElements = 0
  Object = -> Cylinder
  OutputCompounding = 1
  PlacementsTo = -> Join
  Referencing = 0
  Type = lattice2PopulateCopies.LatticePopulateCopies
  isLattice = 0
FEATURE [Part::MultiFuse] Fusion
  Shapes = -> [Populate]
FEATURE [PartDesign::Body] Body001
  AllowCompound = false
  Origin = -> Origin001
FEATURE [PartDesign::Boolean] Boolean
  BaseFeature = -> Pocket003
  Group = -> [Fusion]
  Suppressed = false
  Type = 1
  UsePlacement = true
FEATURE [PartDesign::CoordinateSystem] Local_CS  label="base_LCS"
  AttacherType = Attacher::AttachEngine3D
  AttachmentSupport = -> [XY_Plane]
  MapMode = 5
FEATURE [PartDesign::CoordinateSystem] Local_CS001  label="top_LCS"
  AttacherType = Attacher::AttachEngine3D
  AttachmentOffset = pos=(0,0,84) rot=(0,0,1;0rad)
  AttachmentSupport = -> [XY_Plane]
  MapMode = 5
  Placement = pos=(0,0,84) rot=(0,0,1;0rad)
FEATURE [PartDesign::Body] Body  label="top"
  AllowCompound = false
  Group = -> [Binder001,BaseBend,Sketch,Pocket,Sketch001,Sketch002,Pocket001,Pocket002,Mirrored,Sketch003,Pocket003,Boolean,Local_CS,Local_CS001]
  Origin = -> Origin
  Tip = -> Boolean
